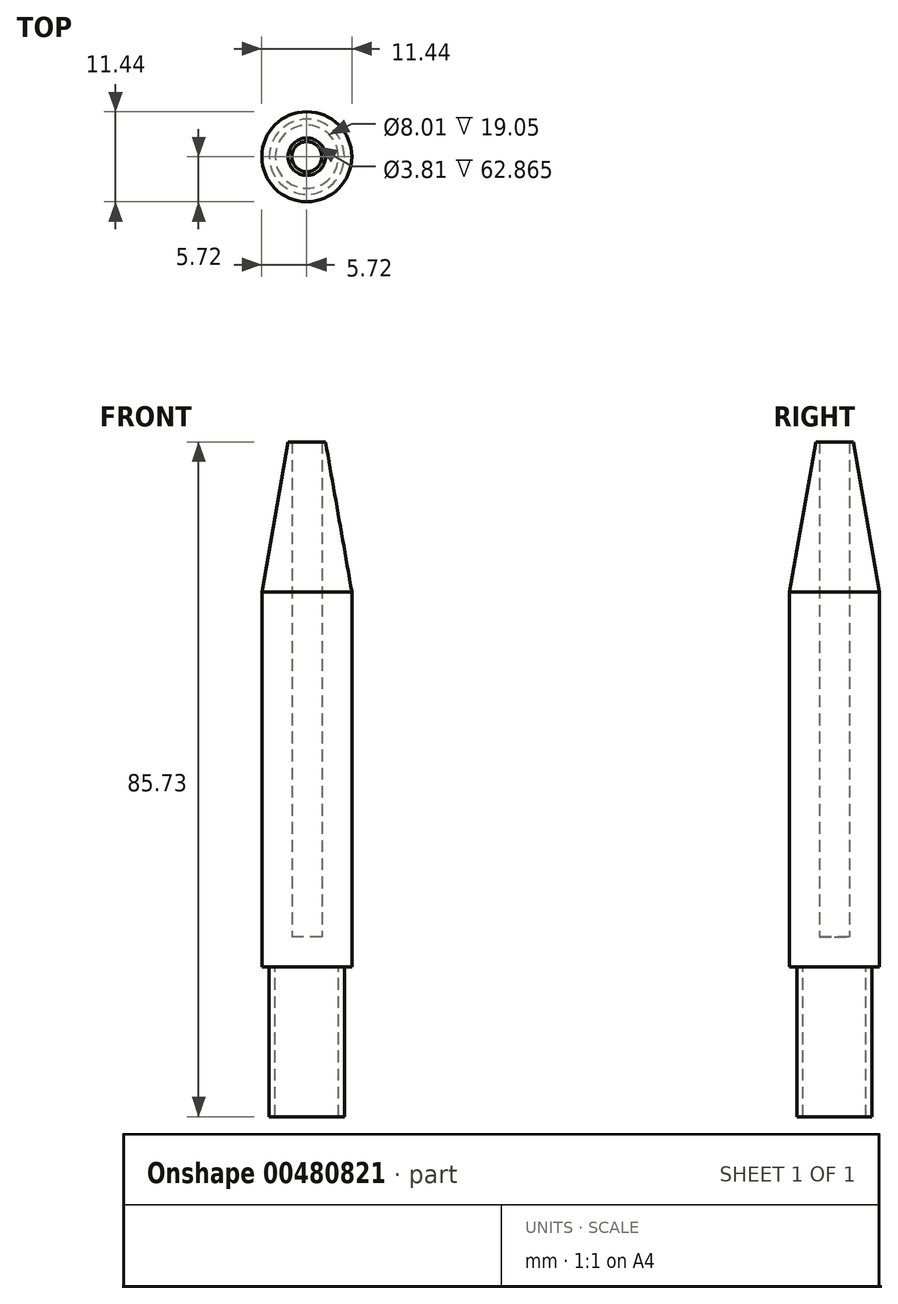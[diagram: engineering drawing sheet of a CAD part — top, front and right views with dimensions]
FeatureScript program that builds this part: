
annotation { "Feature Type Name" : "Feature", "Feature Type Description" : "" }
export const myFeature = defineFeature(function(context is Context, id is Id, definition is map)
    precondition{}
    {
        {
            var Q0;
            Q0=qCreatedBy(makeId("Top.planeOp"),FACE);
            var sketch = newSketch(context, id + "F0", { "sketchPlane" : qUnion([Q0])});
            skCircle(sketch, "E0", {"center": v(0, 0) * mm, "radius": 3.18 * mm});
            skSolve(sketch);
        }
        {
            var Q0;
            Q0=makeQuery(id+"F0.imprint","IMPRINT",FACE,{"disambiguationData":[TD([[makeQuery(id+"F0.imprint","IMPRINT",EDGE,{"derivedFrom":sQuery(id+"F0.wireOp",EDGE,"E0")}),1.0]])]});
            extrude(context, id + "F1", {"entities" : qUnion([Q0]), "depth" : 12.7 * mm});
        }
        {
            var Q0;
            Q0=makeQuery(id+"F1.opExtrude","CAP_FACE",FACE,{"disambiguationData":[OSD([sQuery(id+"F0.wireOp",EDGE,"E0")])],"isStart":false});
            var sketch = newSketch(context, id + "F2", { "sketchPlane" : qUnion([Q0])});
            skCircle(sketch, "E1", {"center": v(0, 0) * mm, "radius": 2.67 * mm});
            skSolve(sketch);
        }
        {
            var Q0;
            Q0=makeQuery(id+"F2.imprint","IMPRINT",FACE,{"disambiguationData":[TD([[makeQuery(id+"F2.imprint","IMPRINT",EDGE,{"derivedFrom":sQuery(id+"F2.wireOp",EDGE,"E1")}),1.0]])]});
            extrude(context, id + "F3", {"entities" : qUnion([Q0]), "operationType" : NewBodyOperationType.REMOVE, "oppositeDirection" : true, "depth" : 25.4 * mm});
        }
        {
            var Q0;
            Q0=makeQuery(id+"F1.opExtrude","CAP_FACE",FACE,{"disambiguationData":[OSD([sQuery(id+"F0.wireOp",EDGE,"E0")])],"isStart":false});
            var sketch = newSketch(context, id + "F4", { "sketchPlane" : qUnion([Q0])});
            skCircle(sketch, "E2", {"center": v(0, 0) * mm, "radius": 3.8 * mm});
            skSolve(sketch);
        }
        {
            var Q0;
            Q0 = qSketchRegion(id + "F4", true);
            extrude(context, id + "F5", {"entities" : qUnion([Q0]), "operationType" : NewBodyOperationType.ADD, "depth" : 31.75 * mm});
        }
        {
            var Q0;
            Q0=makeQuery(id+"F5.opExtrude","CAP_FACE",FACE,{"disambiguationData":[OSD([sQuery(id+"F4.wireOp",EDGE,"E2")])],"isStart":false});
            cPlane(context, id + "F6", {"entities" : qUnion([Q0]), "cplaneType" : CPlaneType.OFFSET, "offset" : 12.7 * mm, "width" : 152.4 * mm, "height" : 152.4 * mm});
        }
        {
            var Q0;
            Q0=qCreatedBy(id+"F6.planeOp",FACE);
            var sketch = newSketch(context, id + "F7", { "sketchPlane" : qUnion([Q0])});
            skCircle(sketch, "E3", {"center": v(0, 0) * mm, "radius": 1.59 * mm});
            skSolve(sketch);
        }
        {
            var Q1;
            Q1=makeQuery(id+"F5.opExtrude","CAP_FACE",FACE,{"disambiguationData":[OSD([sQuery(id+"F4.wireOp",EDGE,"E2")])],"isStart":false});
            var Q2;
            Q2=makeQuery(id+"F7.imprint","IMPRINT",FACE,{"disambiguationData":[TD([[makeQuery(id+"F7.imprint","IMPRINT",EDGE,{"derivedFrom":sQuery(id+"F7.wireOp",EDGE,"E3")}),1.0]])]});
            loft(context, id + "F8", {"operationType" : NewBodyOperationType.ADD, "sheetProfilesArray" : [{ "sheetProfileEntities" : qUnion([Q1]) }, { "sheetProfileEntities" : qUnion([Q2]) }]});
        }
        {
            var Q0;
            Q0=makeQuery(id+"F8.opLoft","SWEPT_FACE",FACE,{"disambiguationData":[OSD([sQuery(id+"F4.wireOp",EDGE,"E2"),sQuery(id+"F7.wireOp",EDGE,"E3")])]});
            var Q1;
            Q1=makeQuery(id+"F8.opLoft","CAP_FACE",FACE,{"disambiguationData":[OSD([makeQuery(id+"F7.imprint","IMPRINT",FACE,{"disambiguationData":[TD([[makeQuery(id+"F7.imprint","IMPRINT",EDGE,{"derivedFrom":sQuery(id+"F7.wireOp",EDGE,"E3")}),1.0]])]})])],"isStart":true});
            shell(context, id + "F9", {"entities" : qUnion([Q0, Q1]), "thickness" : 2.54 * mm});
        }
        {
            var Q0;
            Q0=makeQuery(id+"F1.opExtrude","SWEPT_BODY",BODY,{"disambiguationData":[OSD([sQuery(id+"F0.wireOp",EDGE,"E0")])]});
            var Q1;
            Q1=qCreatedBy(makeId("Origin.pointOp"),VERTEX);
            transform(context, id + "F10", {"entities" : qUnion([Q0]), "transformType" : TransformType.SCALE_UNIFORMLY, "scale" : 1.5, "scalePoint" : qUnion([Q1]), "makeCopy" : false});
        }
    });
